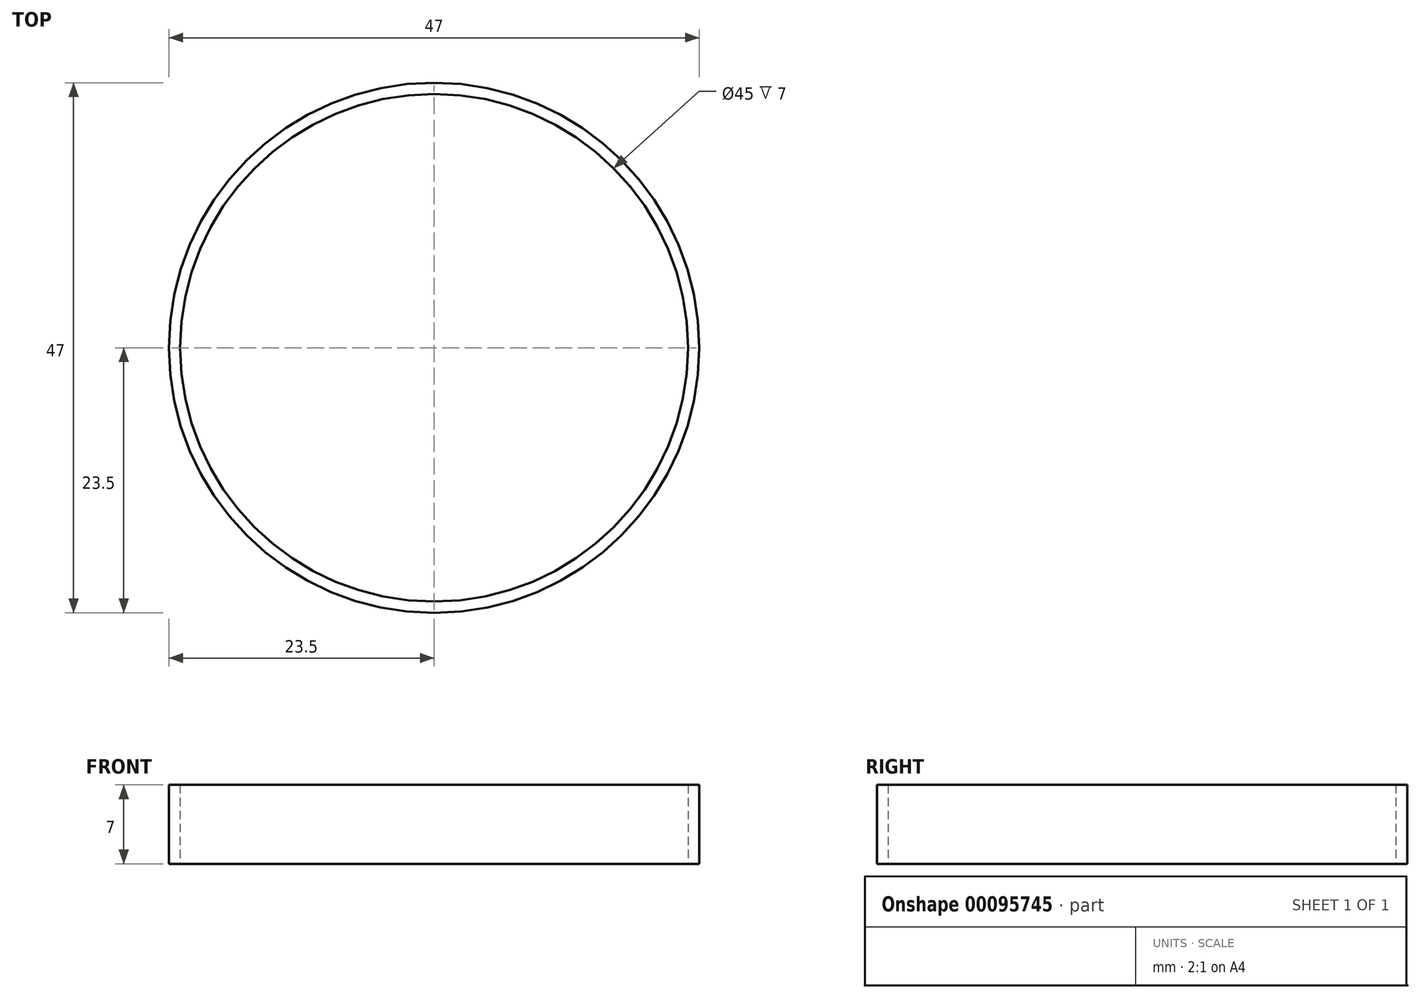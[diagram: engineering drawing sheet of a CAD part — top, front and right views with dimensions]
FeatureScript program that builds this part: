
annotation { "Feature Type Name" : "Feature", "Feature Type Description" : "" }
export const myFeature = defineFeature(function(context is Context, id is Id, definition is map)
    precondition{}
    {
        {
            var Q0;
            Q0=qCreatedBy(makeId("Top.planeOp"),FACE);
            var sketch = newSketch(context, id + "F0", { "sketchPlane" : qUnion([Q0])});
            skCircle(sketch, "E0", {"center": v(0, 0) * mm, "radius": 23.5 * mm});
            skCircle(sketch, "E1", {"center": v(0, 0) * mm, "radius": 22.5 * mm});
            skSolve(sketch);
        }
        {
            var Q0;
            Q0=makeQuery(id+"F0.imprint","IMPRINT",FACE,{"disambiguationData":[TD([[makeQuery(id+"F0.imprint","IMPRINT",EDGE,{"derivedFrom":sQuery(id+"F0.wireOp",EDGE,"E0")}),1.0]])]});
            extrude(context, id + "F1", {"entities" : qUnion([Q0]), "depth" : 7 * mm});
        }
    });
